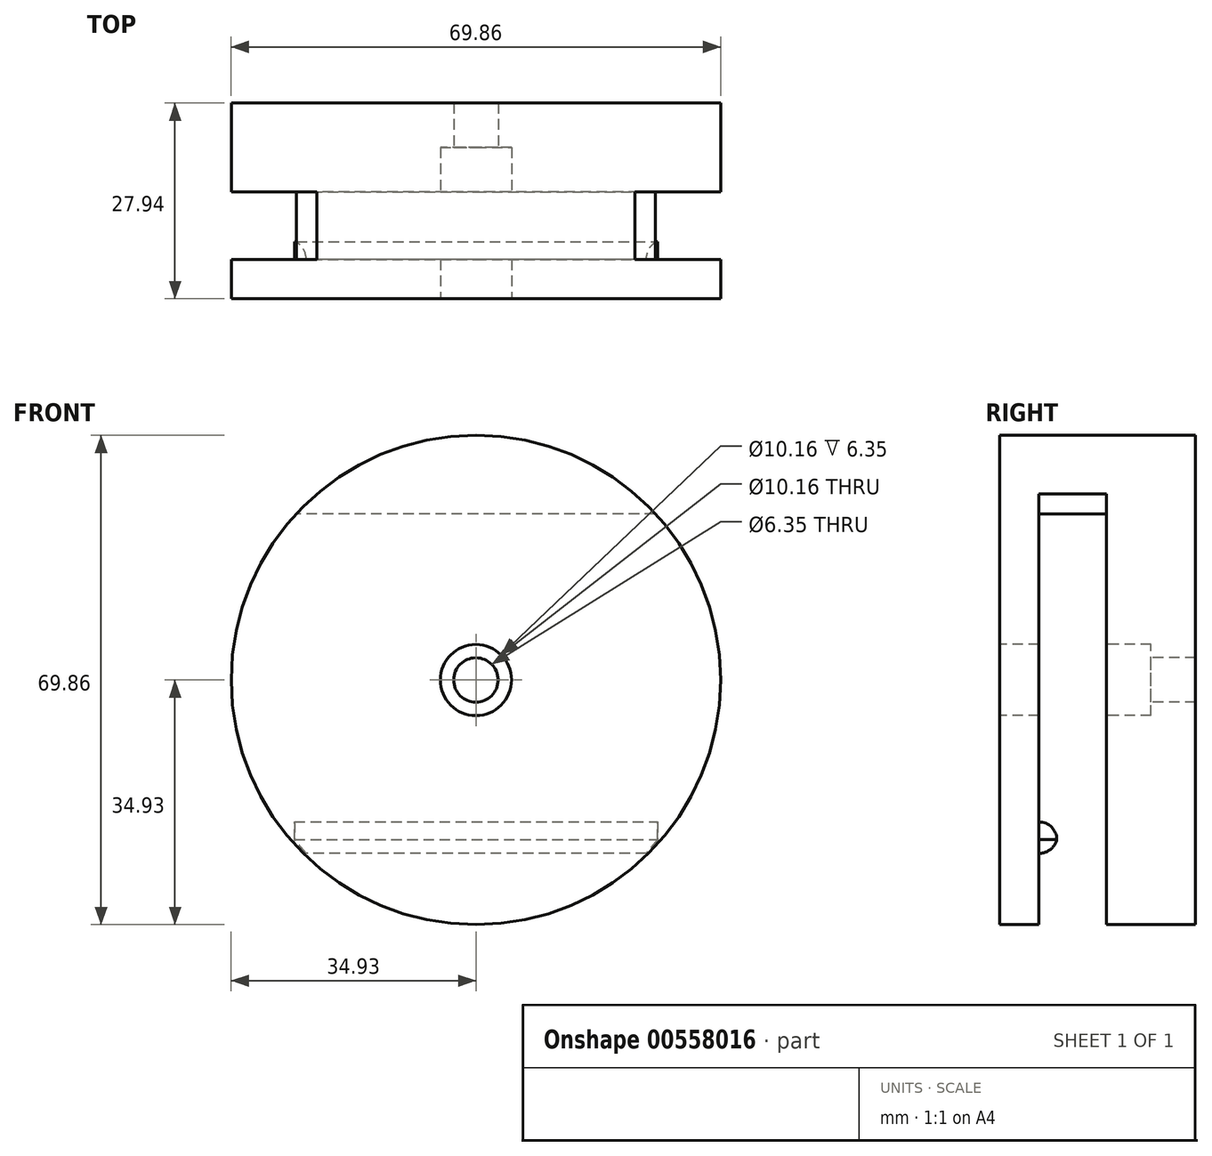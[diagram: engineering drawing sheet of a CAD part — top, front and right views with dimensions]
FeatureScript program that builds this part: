
annotation { "Feature Type Name" : "Feature", "Feature Type Description" : "" }
export const myFeature = defineFeature(function(context is Context, id is Id, definition is map)
    precondition{}
    {
        {
            var Q0;
            Q0=qCreatedBy(makeId("Front.planeOp"),FACE);
            var sketch = newSketch(context, id + "F0", { "sketchPlane" : qUnion([Q0])});
            skCircle(sketch, "E0", {"center": v(0, 0) * mm, "radius": 34.93 * mm});
            skSolve(sketch);
        }
        {
            var Q0;
            Q0 = qSketchRegion(id + "F0", true);
            extrude(context, id + "F1", {"entities" : qUnion([Q0]), "depth" : 12.7 * mm, "offsetDistance" : 25.4 * mm});
        }
        {
            var Q0;
            Q0=makeQuery(id+"F1.opExtrude","CAP_FACE",FACE,{"disambiguationData":[OSD([sQuery(id+"F0.wireOp",EDGE,"E0")])],"isStart":false});
            var sketch = newSketch(context, id + "F2", { "sketchPlane" : qUnion([Q0])});
            skCircle(sketch, "E1", {"center": v(0, 0) * mm, "radius": 5.08 * mm});
            skSolve(sketch);
        }
        {
            var Q0;
            Q0 = qSketchRegion(id + "F2", true);
            extrude(context, id + "F3", {"entities" : qUnion([Q0]), "operationType" : NewBodyOperationType.REMOVE, "oppositeDirection" : true, "depth" : 6.35 * mm, "offsetDistance" : 25.4 * mm});
        }
        {
            var Q0;
            Q0=makeQuery(id+"F1.opExtrude","CAP_FACE",FACE,{"disambiguationData":[OSD([sQuery(id+"F0.wireOp",EDGE,"E0")])],"isStart":false});
            var sketch = newSketch(context, id + "F4", { "sketchPlane" : qUnion([Q0])});
            skLineSegment(sketch, "E2", {"start": v(-22.68, 26.56) * mm, "end": v(22.68, 26.56) * mm});
            skLineSegment(sketch, "E3", {"start": v(22.68, 26.56) * mm, "end": v(25.63, 23.73) * mm});
            skLineSegment(sketch, "E4", {"start": v(25.63, 23.73) * mm, "end": v(-25.63, 23.73) * mm});
            skLineSegment(sketch, "E5", {"start": v(-25.63, 23.73) * mm, "end": v(-22.68, 26.56) * mm});
            skSolve(sketch);
        }
        {
            var Q0;
            Q0=makeQuery(id+"F4.imprint","IMPRINT",FACE,{"disambiguationData":[TD([[makeQuery(id+"F4.imprint","IMPRINT",EDGE,{"derivedFrom":sQuery(id+"F4.wireOp",EDGE,"E2")}),-1.0]])]});
            extrude(context, id + "F5", {"entities" : qUnion([Q0]), "operationType" : NewBodyOperationType.ADD, "depth" : 15.24 * mm, "offsetDistance" : 25.4 * mm});
        }
        {
            var Q0;
            {var subQ0=sQuery(id+"F0.wireOp",EDGE,"E0");var subQ1=makeQuery(id+"F1.opExtrude","CAP_FACE",FACE,{"disambiguationData":[OSD([subQ0])],"isStart":false});Q0=makeQuery(id+"F5.boolean.opBoolean","SPLIT",FACE,{"disambiguationData":[TD([makeQuery(id+"F1.opExtrude","SWEPT_FACE",FACE,{"disambiguationData":[OSD([subQ0])]}),subQ1,makeQuery(id+"F5.opExtrude","SWEPT_FACE",FACE,{"disambiguationData":[OSD([sQuery(id+"F4.wireOp",EDGE,"E2")])]}),makeQuery(id+"F5.opExtrude","SWEPT_FACE",FACE,{"disambiguationData":[OSD([sQuery(id+"F4.wireOp",EDGE,"E3")])]}),makeQuery(id+"F5.opExtrude","SWEPT_FACE",FACE,{"disambiguationData":[OSD([sQuery(id+"F4.wireOp",EDGE,"E5")])]})])],"derivedFrom":subQ1});}
            extrude(context, id + "F6", {"entities" : qUnion([Q0]), "operationType" : NewBodyOperationType.ADD, "depth" : 15.24 * mm, "offsetDistance" : 25.4 * mm});
        }
        {
            var Q0;
            Q0=makeQuery(id+"F6.boolean.opBoolean","MERGE",FACE,{"derivedFrom":[makeQuery(id+"F5.opExtrude","CAP_FACE",FACE,{"disambiguationData":[OSD([sQuery(id+"F4.wireOp",EDGE,"E2"),sQuery(id+"F4.wireOp",EDGE,"E3"),sQuery(id+"F4.wireOp",EDGE,"E4"),sQuery(id+"F4.wireOp",EDGE,"E5")])],"isStart":false}),makeQuery(id+"F6.opExtrude","CAP_FACE",FACE,{"disambiguationData":[OSD([sQuery(id+"F0.wireOp",EDGE,"E0")])],"isStart":false})]});
            var sketch = newSketch(context, id + "F7", { "sketchPlane" : qUnion([Q0])});
            skCircle(sketch, "E6", {"center": v(0, 0) * mm, "radius": 34.93 * mm});
            skSolve(sketch);
        }
        {
            var Q0;
            Q0 = qSketchRegion(id + "F7", true);
            extrude(context, id + "F8", {"entities" : qUnion([Q0]), "operationType" : NewBodyOperationType.ADD, "oppositeDirection" : true, "depth" : 5.6 * mm, "offsetDistance" : 25.4 * mm});
        }
        {
            var Q0;
            Q0=makeQuery(id+"F8.boolean.opBoolean","MERGE",FACE,{"derivedFrom":[makeQuery(id+"F6.boolean.opBoolean","MERGE",FACE,{"derivedFrom":[makeQuery(id+"F5.opExtrude","CAP_FACE",FACE,{"disambiguationData":[OSD([sQuery(id+"F4.wireOp",EDGE,"E2"),sQuery(id+"F4.wireOp",EDGE,"E3"),sQuery(id+"F4.wireOp",EDGE,"E4"),sQuery(id+"F4.wireOp",EDGE,"E5")])],"isStart":false}),makeQuery(id+"F6.opExtrude","CAP_FACE",FACE,{"disambiguationData":[OSD([sQuery(id+"F0.wireOp",EDGE,"E0")])],"isStart":false})]}),makeQuery(id+"F8.opExtrude","CAP_FACE",FACE,{"disambiguationData":[OSD([sQuery(id+"F7.wireOp",EDGE,"E6")])],"isStart":true})]});
            var sketch = newSketch(context, id + "F9", { "sketchPlane" : qUnion([Q0])});
            skCircle(sketch, "E7", {"center": v(0, 0) * mm, "radius": 5.08 * mm});
            skSolve(sketch);
        }
        {
            var Q0;
            Q0 = qSketchRegion(id + "F9", true);
            extrude(context, id + "F10", {"entities" : qUnion([Q0]), "operationType" : NewBodyOperationType.REMOVE, "oppositeDirection" : true, "depth" : 6.35 * mm, "offsetDistance" : 25.4 * mm});
        }
        {
            var Q0;
            {var subQ0=sQuery(id+"F7.wireOp",EDGE,"E6");var subQ1=makeQuery(id+"F8.opExtrude","CAP_FACE",FACE,{"disambiguationData":[OSD([subQ0])],"isStart":false});var subQ2=sQuery(id+"F0.wireOp",EDGE,"E0");Q0=makeQuery(id+"F8.boolean.opBoolean","SPLIT",FACE,{"disambiguationData":[TD([makeQuery(id+"F1.opExtrude","SWEPT_FACE",FACE,{"disambiguationData":[OSD([subQ2])]}),makeQuery(id+"F5.opExtrude","SWEPT_FACE",FACE,{"disambiguationData":[OSD([sQuery(id+"F4.wireOp",EDGE,"E3")])]}),makeQuery(id+"F5.opExtrude","SWEPT_FACE",FACE,{"disambiguationData":[OSD([sQuery(id+"F4.wireOp",EDGE,"E4")])]}),makeQuery(id+"F5.opExtrude","SWEPT_FACE",FACE,{"disambiguationData":[OSD([sQuery(id+"F4.wireOp",EDGE,"E5")])]}),makeQuery(id+"F6.opExtrude","SWEPT_FACE",FACE,{"disambiguationData":[OSD([subQ2])]}),makeQuery(id+"F8.opExtrude","SWEPT_FACE",FACE,{"disambiguationData":[OSD([subQ0])]}),subQ1])],"derivedFrom":subQ1});}
            var sketch = newSketch(context, id + "F11", { "sketchPlane" : qUnion([Q0])});
            skSolve(sketch);
        }
        {
            var Q0;
            {var subQ0=sQuery(id+"F7.wireOp",EDGE,"E6");var subQ1=makeQuery(id+"F8.opExtrude","CAP_FACE",FACE,{"disambiguationData":[OSD([subQ0])],"isStart":false});var subQ2=makeQuery(id+"F5.opExtrude","SWEPT_FACE",FACE,{"disambiguationData":[OSD([sQuery(id+"F4.wireOp",EDGE,"E4")])]});Q0=makeQuery(id+"F11.imprint","IMPRINT",FACE,{"disambiguationData":[TD([[makeQuery(id+"F11.imprint","IMPRINT",EDGE,{"derivedFrom":makeQuery(id+"F8.boolean.opBoolean","INTERSECT",EDGE,{"derivedFrom":[subQ2,subQ1]})}),-1.0]])]});}
            var sketch = newSketch(context, id + "F12", { "sketchPlane" : qUnion([Q0])});
            skLineSegment(sketch, "E8", {"start": v(-24.3, -24.73) * mm, "end": v(24.24, -24.73) * mm});
            skLineSegment(sketch, "E9", {"start": v(24.24, -24.73) * mm, "end": v(25.89, -22.8) * mm});
            skLineSegment(sketch, "E10", {"start": v(25.89, -22.8) * mm, "end": v(-25.95, -22.8) * mm});
            skLineSegment(sketch, "E11", {"start": v(-25.95, -22.8) * mm, "end": v(-24.3, -24.73) * mm});
            skSolve(sketch);
        }
        {
            var Q0;
            Q0 = qSketchRegion(id + "F12", true);
            extrude(context, id + "F13", {"entities" : qUnion([Q0]), "operationType" : NewBodyOperationType.ADD, "depth" : 2.54 * mm, "offsetDistance" : 25.4 * mm});
        }
        {
            var Q0;
            Q0=makeQuery(id+"F13.opExtrude","CAP_EDGE",EDGE,{"disambiguationData":[OSD([sQuery(id+"F12.wireOp",EDGE,"E8")])],"isStart":false});
            fillet(context, id + "F14", {"entities" : qUnion([Q0]), "radius" : 2.54 * mm, "tangentPropagation" : true, "allowEdgeOverflow" : false});
        }
        {
            var Q0;
            Q0=makeQuery(id+"F13.opExtrude","SWEPT_FACE",FACE,{"disambiguationData":[OSD([sQuery(id+"F12.wireOp",EDGE,"E10")])]});
            extrude(context, id + "F15", {"entities" : qUnion([Q0]), "operationType" : NewBodyOperationType.ADD, "depth" : 2.54 * mm, "offsetDistance" : 25.4 * mm});
        }
        {
            var Q0;
            Q0=makeQuery(id+"F15.opExtrude","CAP_EDGE",EDGE,{"disambiguationData":[OSD([sQuery(id+"F12.wireOp",EDGE,"E8"),sQuery(id+"F12.wireOp",EDGE,"E10")])],"isStart":false});
            fillet(context, id + "F16", {"entities" : qUnion([Q0]), "radius" : 2.54 * mm, "tangentPropagation" : true, "allowEdgeOverflow" : false});
        }
        {
            var Q0;
            {var subQ0=sQuery(id+"F0.wireOp",EDGE,"E0");var subQ1=sQuery(id+"F7.wireOp",EDGE,"E6");var subQ2=makeQuery(id+"F8.opExtrude","CAP_FACE",FACE,{"disambiguationData":[OSD([subQ1])],"isStart":false});Q0=makeQuery(id+"F11.imprint","IMPRINT",FACE,{"disambiguationData":[TD([[makeQuery(id+"F11.imprint","IMPRINT",EDGE,{"derivedFrom":makeQuery(id+"F10.boolean.opBoolean","INTERSECT",EDGE,{"derivedFrom":[makeQuery(id+"F8.boolean.opBoolean","SPLIT",FACE,{"disambiguationData":[TD([makeQuery(id+"F1.opExtrude","SWEPT_FACE",FACE,{"disambiguationData":[OSD([subQ0])]}),makeQuery(id+"F5.opExtrude","SWEPT_FACE",FACE,{"disambiguationData":[OSD([sQuery(id+"F4.wireOp",EDGE,"E3")])]}),makeQuery(id+"F5.opExtrude","SWEPT_FACE",FACE,{"disambiguationData":[OSD([sQuery(id+"F4.wireOp",EDGE,"E4")])]}),makeQuery(id+"F5.opExtrude","SWEPT_FACE",FACE,{"disambiguationData":[OSD([sQuery(id+"F4.wireOp",EDGE,"E5")])]}),makeQuery(id+"F6.opExtrude","SWEPT_FACE",FACE,{"disambiguationData":[OSD([subQ0])]}),makeQuery(id+"F8.opExtrude","SWEPT_FACE",FACE,{"disambiguationData":[OSD([subQ1])]}),subQ2])],"derivedFrom":subQ2}),makeQuery(id+"F10.opExtrude","SWEPT_FACE",FACE,{"disambiguationData":[OSD([sQuery(id+"F9.wireOp",EDGE,"E7")])]})]})}),-1.0]])]});}
            var sketch = newSketch(context, id + "F17", { "sketchPlane" : qUnion([Q0])});
            skCircle(sketch, "E12", {"center": v(0, 0) * mm, "radius": 3.18 * mm});
            skSolve(sketch);
        }
        {
            var Q0;
            Q0 = qSketchRegion(id + "F17", true);
            extrude(context, id + "F18", {"entities" : qUnion([Q0]), "operationType" : NewBodyOperationType.REMOVE, "depth" : 25.4 * mm, "offsetDistance" : 25.4 * mm});
        }
    });
